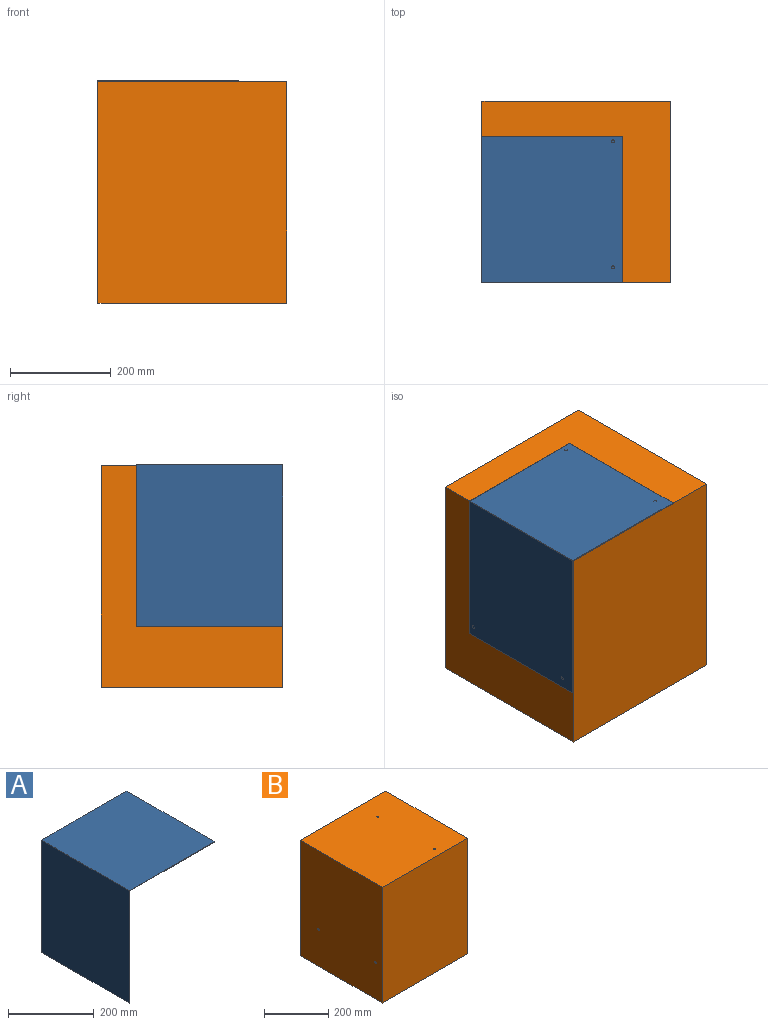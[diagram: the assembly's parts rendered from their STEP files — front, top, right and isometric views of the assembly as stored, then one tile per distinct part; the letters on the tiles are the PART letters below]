
ASSEMBLY  parts=2 mates=1
PART A: 8 faces, bbox 281.6x290x321.6 mm
  f0: plane 320x290mm, normal (1,0,0), area 92800mm2, adj f1,f5,f6,f7
  f1: plane 290x280mm, normal (0,0,-1), area 81200mm2, adj f0,f2,f6,f7
  f2: plane 290x1.6mm, normal (1,0,0), area 464mm2, adj f1,f3,f6,f7
  f3: plane 290x281.6mm, normal (0,0,1), area 81664mm2, adj f2,f4,f6,f7
  f4: plane 321.6x290mm, normal (-1,0,0), area 93264mm2, adj f3,f5,f6,f7
  f5: plane 290x1.6mm, normal (0,0,-1), area 464mm2, adj f0,f4,f6,f7
  f6: plane 321.6x281.6mm, normal (0,-1,0), area 962.6mm2, adj f0,f1,f2,f3,f4,f5
  f7: plane 321.6x281.6mm, normal (0,1,0), area 962.6mm2, adj f0,f1,f2,f3,f4,f5
PART B: 14 faces, bbox 375x360x440 mm
  f0: cylinder r=3mm len=260mm, axis (-1,0,0), area 4864.9mm2, adj f4,f12,f13
  f1: cylinder r=3mm len=115mm, axis (-1,0,0), area 2131.7mm2, adj f6,f12,f13
  f2: cylinder r=3mm len=260mm, axis (-1,0,0), area 4864.9mm2, adj f4,f10,f11
  f3: cylinder r=3mm len=115mm, axis (-1,0,0), area 2131.7mm2, adj f6,f10,f11
  f4: plane 440x360mm, normal (-1,0,0), area 158343.5mm2, adj f0,f2,f5,f7,f8,f9
  f5: plane 440x375mm, normal (0,-1,0), area 165000mm2, adj f4,f6,f8,f9
  f6: plane 440x360mm, normal (1,0,0), area 158343.5mm2, adj f1,f3,f5,f7,f8,f9
  f7: plane 440x375mm, normal (0,1,0), area 165000mm2, adj f4,f6,f8,f9
  f8: plane 375x360mm, normal (0,0,1), area 134943.5mm2, adj f4,f5,f6,f7,f10,f12
  f9: plane 375x360mm, normal (0,0,-1), area 134943.5mm2, adj f4,f5,f6,f7,f11,f13
  f10: cylinder r=3mm len=300mm, axis (0,0,1), area 5618.9mm2, adj f2,f3,f8
  f11: cylinder r=3mm len=140mm, axis (0,0,1), area 2602.9mm2, adj f2,f3,f9
  f12: cylinder r=3mm len=300mm, axis (0,0,1), area 5618.9mm2, adj f0,f1,f8
  f13: cylinder r=3mm len=140mm, axis (0,0,1), area 2602.9mm2, adj f0,f1,f9
PLACE A rot(axis=(-1,0,0),0deg) t=(-596.52,396.02,-48.38)mm
PLACE B rot(axis=(-1,0,0),0deg) t=(-49.19,313.66,-168.38)mm
MATE fastened A.f1 <-> B.f8  axis (0,0,-1) through (-49.19,106.02,271.62)mm
